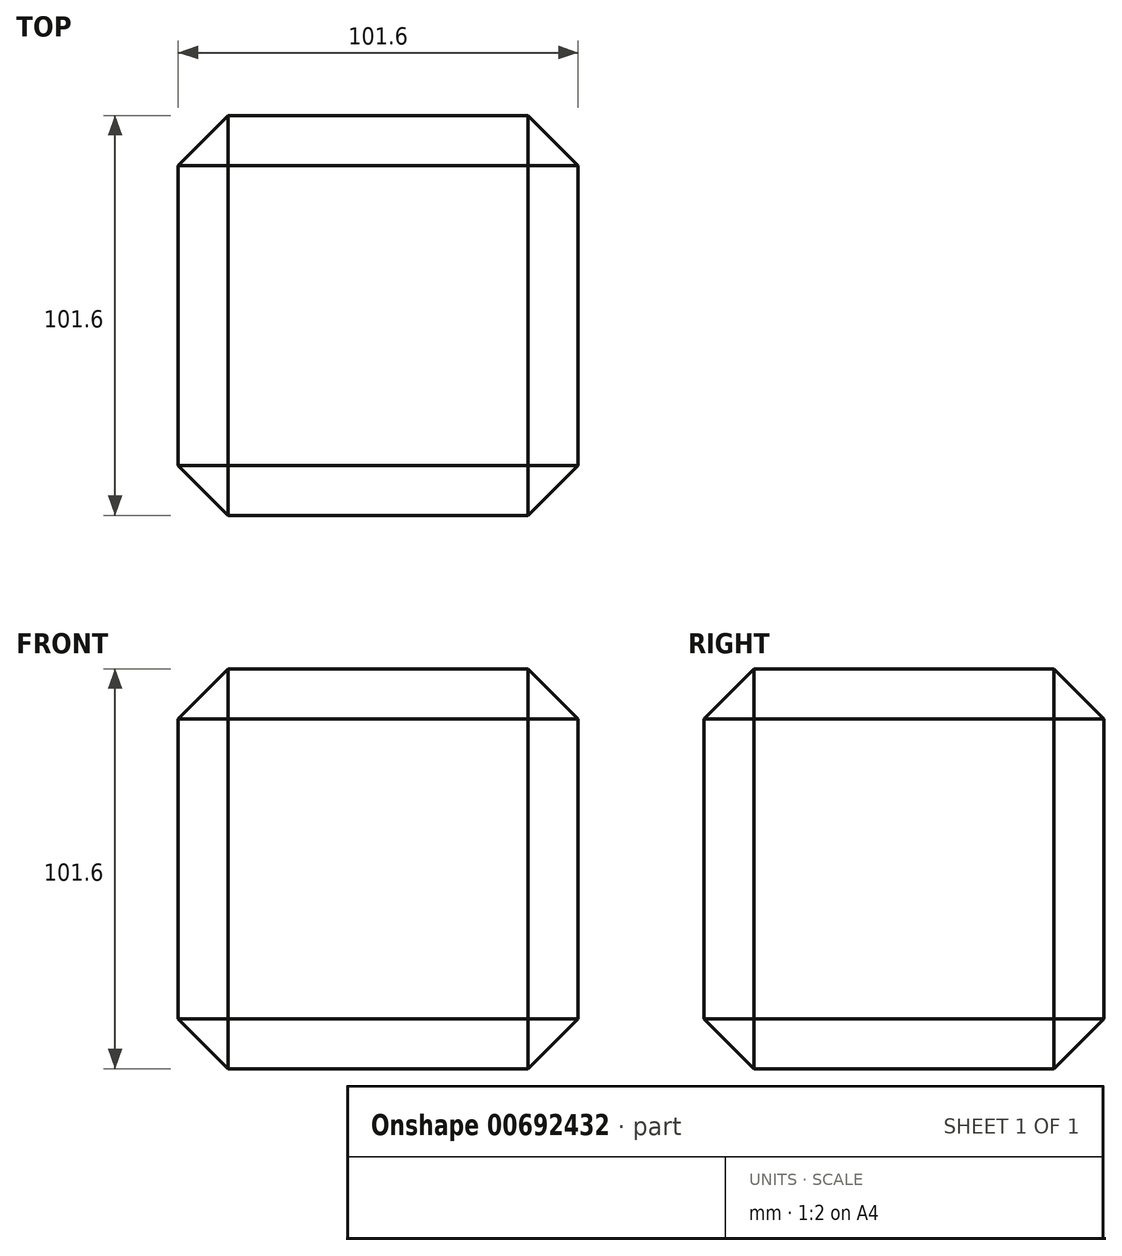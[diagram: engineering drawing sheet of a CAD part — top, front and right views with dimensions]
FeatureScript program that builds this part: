
annotation { "Feature Type Name" : "Feature", "Feature Type Description" : "" }
export const myFeature = defineFeature(function(context is Context, id is Id, definition is map)
    precondition{}
    {
        {
            var Q0;
            Q0=qCreatedBy(makeId("Front.planeOp"),FACE);
            var sketch = newSketch(context, id + "F0", { "sketchPlane" : qUnion([Q0])});
            skLineSegment(sketch, "E0.bottom", {"start": v(50.8, 50.8) * mm, "end": v(-50.8, 50.8) * mm});
            skLineSegment(sketch, "E0.top", {"start": v(50.8, -50.8) * mm, "end": v(-50.8, -50.8) * mm});
            skLineSegment(sketch, "E0.left", {"start": v(50.8, 50.8) * mm, "end": v(50.8, -50.8) * mm});
            skLineSegment(sketch, "E0.right", {"start": v(-50.8, 50.8) * mm, "end": v(-50.8, -50.8) * mm});
            skPoint(sketch, "E0.middle", {"position": v(0, 0) * mm});
            skSolve(sketch);
        }
        {
            var Q0;
            Q0=makeQuery(id+"F0.imprint","IMPRINT",FACE,{"disambiguationData":[TD([[makeQuery(id+"F0.imprint","IMPRINT",EDGE,{"derivedFrom":sQuery(id+"F0.wireOp",EDGE,"E0.bottom")}),1.0]])]});
            extrude(context, id + "F1", {"entities" : qUnion([Q0]), "endBound" : BoundingType.SYMMETRIC, "depth" : 101.6 * mm, "offsetDistance" : 25.4 * mm});
        }
        {
            var Q0;
            Q0=makeQuery(id+"F1.opExtrude","SWEPT_EDGE",EDGE,{"disambiguationData":[OSD([sQuery(id+"F0.wireOp",EDGE,"E0.bottom"),sQuery(id+"F0.wireOp",EDGE,"E0.left")])]});
            var Q1;
            Q1=makeQuery(id+"F1.opExtrude","CAP_EDGE",EDGE,{"disambiguationData":[OSD([sQuery(id+"F0.wireOp",EDGE,"E0.bottom")])],"isStart":false});
            var Q2;
            Q2=makeQuery(id+"F1.opExtrude","SWEPT_EDGE",EDGE,{"disambiguationData":[OSD([sQuery(id+"F0.wireOp",EDGE,"E0.bottom"),sQuery(id+"F0.wireOp",EDGE,"E0.right")])]});
            var Q3;
            Q3=makeQuery(id+"F1.opExtrude","CAP_EDGE",EDGE,{"disambiguationData":[OSD([sQuery(id+"F0.wireOp",EDGE,"E0.bottom")])],"isStart":true});
            var Q4;
            Q4=makeQuery(id+"F1.opExtrude","SWEPT_EDGE",EDGE,{"disambiguationData":[OSD([sQuery(id+"F0.wireOp",EDGE,"E0.top"),sQuery(id+"F0.wireOp",EDGE,"E0.left")])]});
            var Q5;
            Q5=makeQuery(id+"F1.opExtrude","CAP_EDGE",EDGE,{"disambiguationData":[OSD([sQuery(id+"F0.wireOp",EDGE,"E0.left")])],"isStart":false});
            var Q6;
            Q6=makeQuery(id+"F1.opExtrude","CAP_EDGE",EDGE,{"disambiguationData":[OSD([sQuery(id+"F0.wireOp",EDGE,"E0.left")])],"isStart":true});
            var Q7;
            Q7=makeQuery(id+"F1.opExtrude","CAP_EDGE",EDGE,{"disambiguationData":[OSD([sQuery(id+"F0.wireOp",EDGE,"E0.right")])],"isStart":false});
            var Q8;
            Q8=makeQuery(id+"F1.opExtrude","CAP_EDGE",EDGE,{"disambiguationData":[OSD([sQuery(id+"F0.wireOp",EDGE,"E0.top")])],"isStart":false});
            var Q9;
            Q9=makeQuery(id+"F1.opExtrude","CAP_EDGE",EDGE,{"disambiguationData":[OSD([sQuery(id+"F0.wireOp",EDGE,"E0.right")])],"isStart":true});
            var Q10;
            Q10=makeQuery(id+"F1.opExtrude","CAP_EDGE",EDGE,{"disambiguationData":[OSD([sQuery(id+"F0.wireOp",EDGE,"E0.top")])],"isStart":true});
            var Q11;
            Q11=makeQuery(id+"F1.opExtrude","SWEPT_EDGE",EDGE,{"disambiguationData":[OSD([sQuery(id+"F0.wireOp",EDGE,"E0.top"),sQuery(id+"F0.wireOp",EDGE,"E0.right")])]});
            chamfer(context, id + "F2", {"entities" : qUnion([Q0, Q1, Q2, Q3, Q4, Q5, Q6, Q7, Q8, Q9, Q10, Q11]), "width" : 12.7 * mm, "tangentPropagation" : true});
        }
    });
